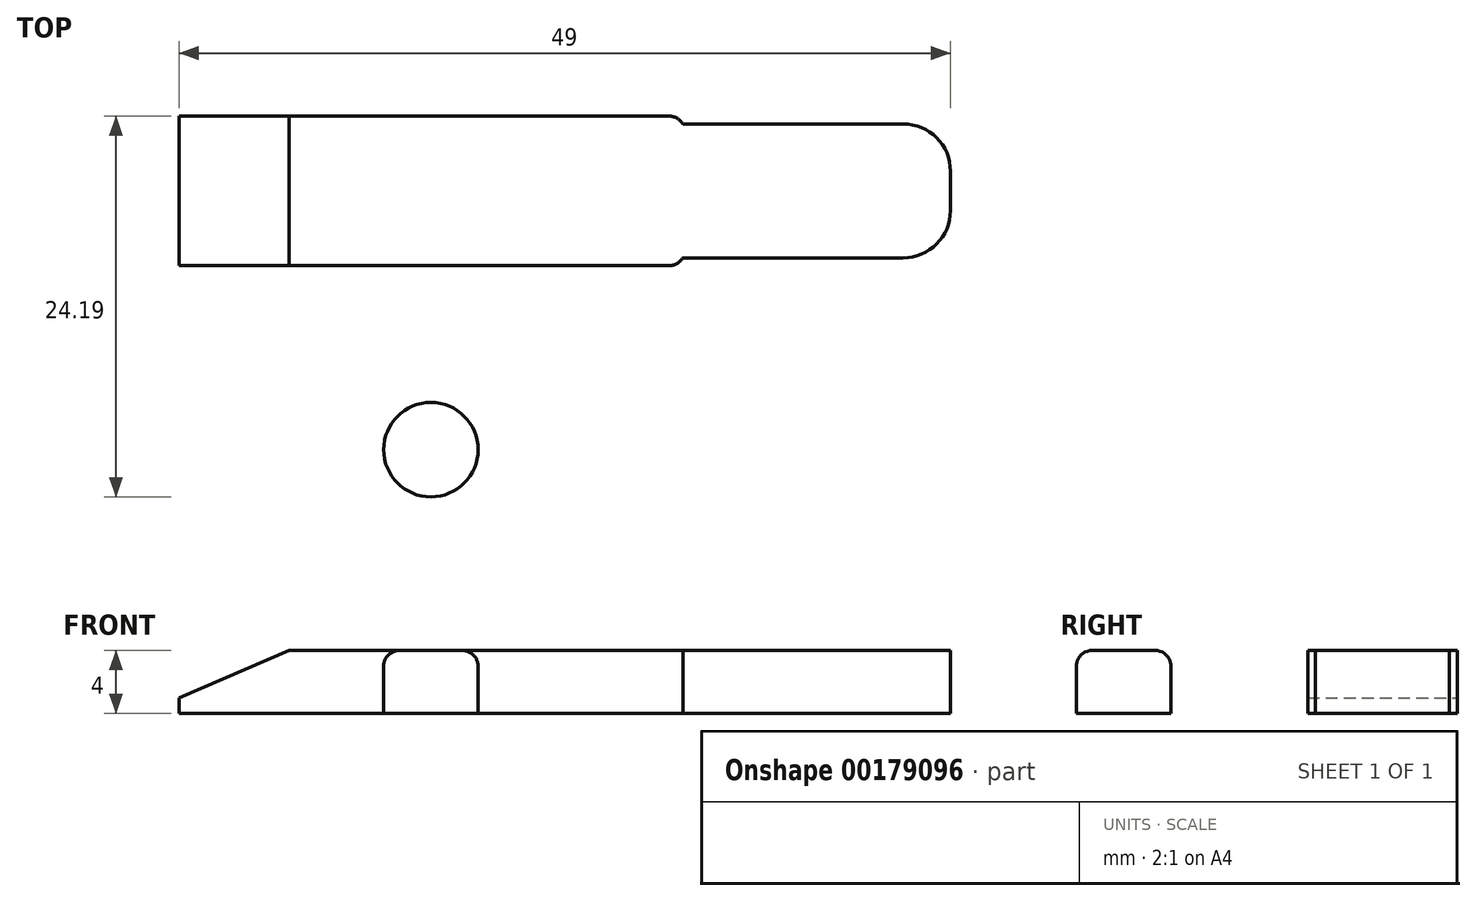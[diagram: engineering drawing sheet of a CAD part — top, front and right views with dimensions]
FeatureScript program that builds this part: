
annotation { "Feature Type Name" : "Feature", "Feature Type Description" : "" }
export const myFeature = defineFeature(function(context is Context, id is Id, definition is map)
    precondition{}
    {
        {
            var Q0;
            Q0=qCreatedBy(makeId("Top.planeOp"),FACE);
            var sketch = newSketch(context, id + "F0", { "sketchPlane" : qUnion([Q0])});
            skLineSegment(sketch, "E0.bottom", {"start": v(16, -4.75) * mm, "end": v(-16, -4.75) * mm});
            skLineSegment(sketch, "E0.top", {"start": v(16, 4.75) * mm, "end": v(-16, 4.75) * mm});
            skLineSegment(sketch, "E0.left", {"start": v(16, -4.75) * mm, "end": v(16, 4.75) * mm});
            skLineSegment(sketch, "E0.right", {"start": v(-16, -4.75) * mm, "end": v(-16, 4.75) * mm});
            skPoint(sketch, "E0.middle", {"position": v(0, 0) * mm});
            skLineSegment(sketch, "E1.bottom", {"start": v(33, -4.25) * mm, "end": v(16, -4.25) * mm});
            skLineSegment(sketch, "E1.top", {"start": v(33, 4.25) * mm, "end": v(16, 4.25) * mm});
            skLineSegment(sketch, "E1.left", {"start": v(33, -4.25) * mm, "end": v(33, 4.25) * mm});
            skLineSegment(sketch, "E1.right", {"start": v(16, -4.25) * mm, "end": v(16, 4.25) * mm});
            skPoint(sketch, "E1.middle", {"position": v(24.5, 0) * mm});
            skCircle(sketch, "E2", {"center": v(0, -16.44) * mm, "radius": 3 * mm});
            skSolve(sketch);
        }
        {
            var Q0;
            {var subQ3=sQuery(id+"F0.wireOp",EDGE,"E0.bottom");Q0=makeQuery(id+"F0.imprint","IMPRINT",FACE,{"disambiguationData":[TD([[makeQuery(id+"F0.imprint","IMPRINT",EDGE,{"derivedFrom":subQ3}),-1.0]])]});}
            var Q1;
            Q1=makeQuery(id+"F0.imprint","IMPRINT",FACE,{"disambiguationData":[TD([[makeQuery(id+"F0.imprint","IMPRINT",EDGE,{"derivedFrom":sQuery(id+"F0.wireOp",EDGE,"E1.bottom")}),-1.0]])]});
            var Q2;
            Q2=makeQuery(id+"F0.imprint","IMPRINT",FACE,{"disambiguationData":[TD([[makeQuery(id+"F0.imprint","IMPRINT",EDGE,{"derivedFrom":sQuery(id+"F0.wireOp",EDGE,"E2")}),1.0]])]});
            extrude(context, id + "F1", {"entities" : qUnion([Q0, Q1, Q2]), "depth" : 4 * mm});
        }
        {
            var Q0;
            Q0=makeQuery(id+"F1.opExtrude","SWEPT_EDGE",EDGE,{"disambiguationData":[OSD([sQuery(id+"F0.wireOp",EDGE,"E1.bottom"),sQuery(id+"F0.wireOp",EDGE,"E1.left")])]});
            var Q1;
            Q1=makeQuery(id+"F1.opExtrude","SWEPT_EDGE",EDGE,{"disambiguationData":[OSD([sQuery(id+"F0.wireOp",EDGE,"E1.top"),sQuery(id+"F0.wireOp",EDGE,"E1.left")])]});
            fillet(context, id + "F2", {"entities" : qUnion([Q0, Q1]), "radius" : 3 * mm, "tangentPropagation" : true, "allowEdgeOverflow" : false});
        }
        {
            var Q0;
            Q0=makeQuery(id+"F1.opExtrude","CAP_EDGE",EDGE,{"disambiguationData":[OSD([sQuery(id+"F0.wireOp",EDGE,"E0.right")])],"isStart":false});
            chamfer(context, id + "F3", {"entities" : qUnion([Q0]), "chamferType" : ChamferType.TWO_OFFSETS, "width1" : 3 * mm, "oppositeDirection" : false, "width2" : 7 * mm, "tangentPropagation" : true});
        }
        {
            var Q0;
            Q0=makeQuery(id+"F1.opExtrude","SWEPT_EDGE",EDGE,{"disambiguationData":[OSD([sQuery(id+"F0.wireOp",EDGE,"E0.bottom"),sQuery(id+"F0.wireOp",EDGE,"E0.left")])]});
            var Q1;
            Q1=makeQuery(id+"F1.opExtrude","SWEPT_EDGE",EDGE,{"disambiguationData":[OSD([sQuery(id+"F0.wireOp",EDGE,"E0.top"),sQuery(id+"F0.wireOp",EDGE,"E0.left")])]});
            var Q2;
            Q2=makeQuery(id+"F1.opExtrude","CAP_EDGE",EDGE,{"disambiguationData":[OSD([sQuery(id+"F0.wireOp",EDGE,"E2")])],"isStart":false});
            fillet(context, id + "F4", {"entities" : qUnion([Q0, Q1, Q2]), "radius" : 1 * mm, "tangentPropagation" : true, "allowEdgeOverflow" : false});
        }
    });
